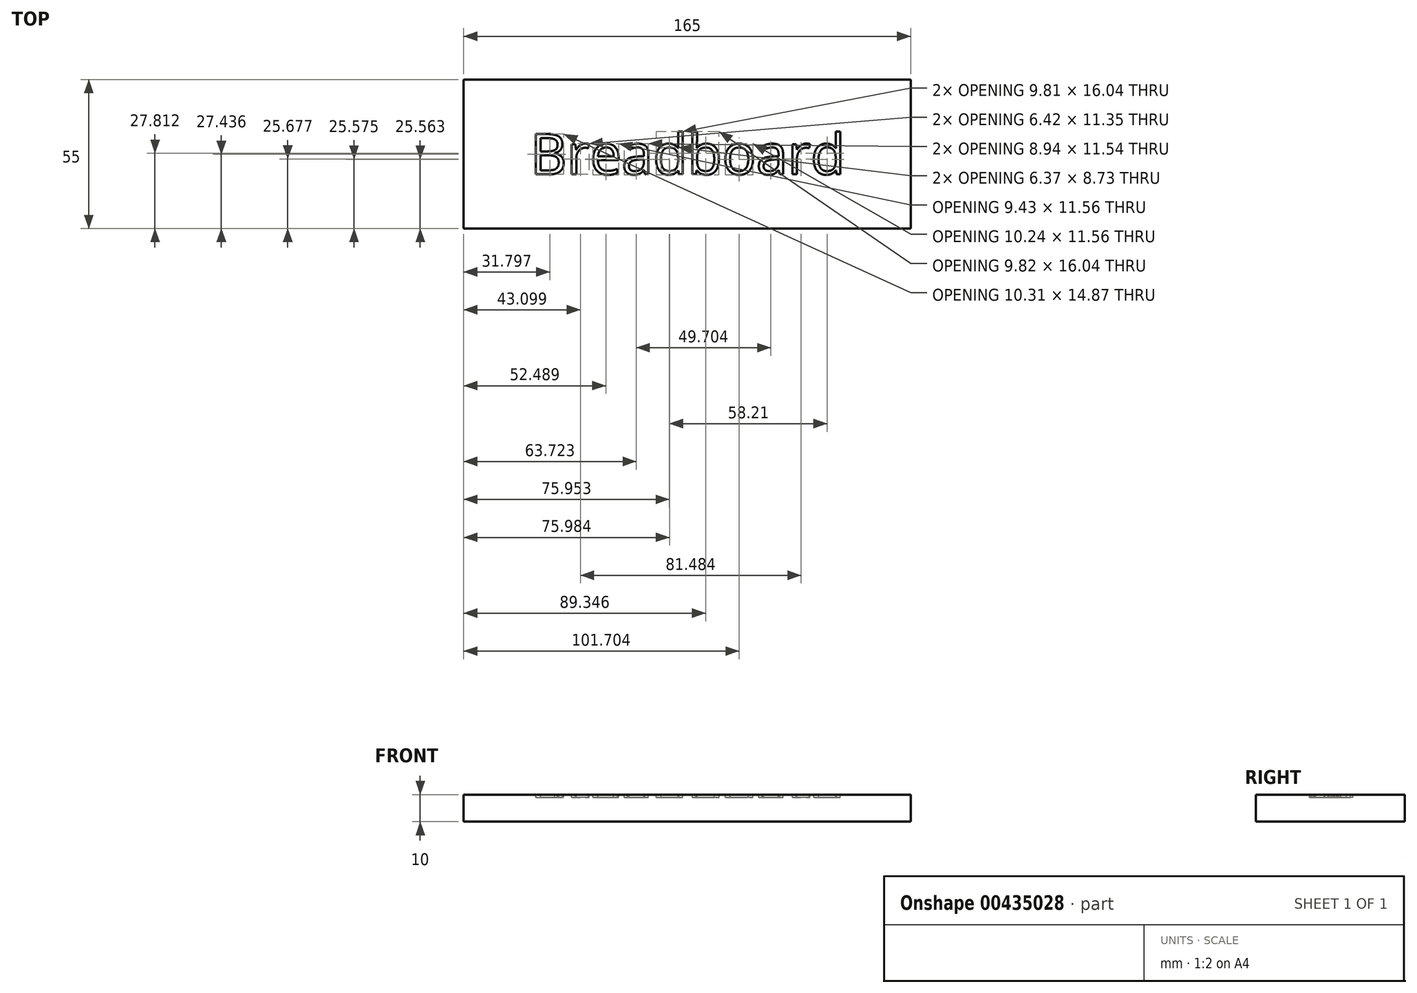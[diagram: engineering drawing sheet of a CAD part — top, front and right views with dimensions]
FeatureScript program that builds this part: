
annotation { "Feature Type Name" : "Feature", "Feature Type Description" : "" }
export const myFeature = defineFeature(function(context is Context, id is Id, definition is map)
    precondition{}
    {
        {
            var Q0;
            Q0=qCreatedBy(makeId("Top.planeOp"),FACE);
            var sketch = newSketch(context, id + "F0", { "sketchPlane" : qUnion([Q0])});
            skLineSegment(sketch, "E0.bottom", {"start": v(82.5, -27.5) * mm, "end": v(-82.5, -27.5) * mm});
            skLineSegment(sketch, "E0.top", {"start": v(82.5, 27.5) * mm, "end": v(-82.5, 27.5) * mm});
            skLineSegment(sketch, "E0.left", {"start": v(82.5, -27.5) * mm, "end": v(82.5, 27.5) * mm});
            skLineSegment(sketch, "E0.right", {"start": v(-82.5, -27.5) * mm, "end": v(-82.5, 27.5) * mm});
            skPoint(sketch, "E0.middle", {"position": v(0, 0) * mm});
            skSolve(sketch);
        }
        {
            var Q0;
            Q0=makeQuery(id+"F0.imprint","IMPRINT",FACE,{"disambiguationData":[TD([[makeQuery(id+"F0.imprint","IMPRINT",EDGE,{"derivedFrom":sQuery(id+"F0.wireOp",EDGE,"E0.bottom")}),-1.0]])]});
            extrude(context, id + "F1", {"entities" : qUnion([Q0]), "depth" : 10 * mm});
        }
        {
            var Q0;
            Q0=makeQuery(id+"F1.opExtrude","CAP_FACE",FACE,{"disambiguationData":[OSD([sQuery(id+"F0.wireOp",EDGE,"E0.bottom"),sQuery(id+"F0.wireOp",EDGE,"E0.top"),sQuery(id+"F0.wireOp",EDGE,"E0.left"),sQuery(id+"F0.wireOp",EDGE,"E0.right")])],"isStart":false});
            var sketch = newSketch(context, id + "F2", { "sketchPlane" : qUnion([Q0])});
            skText(sketch, "E1", { "text": "Breadboard", "fontName": "OpenSans-Regular.ttf"});
            const initialGuessF2  = {"E1": [-0.0579, -0.0075, 1, 0, 0.015]};
            skSetInitialGuess(sketch, initialGuessF2);
            skSolve(sketch);
        }
        {
            var Q0;
            Q0 = qSketchRegion(id + "F2", true);
            extrude(context, id + "F3", {"entities" : qUnion([Q0]), "operationType" : NewBodyOperationType.REMOVE, "oppositeDirection" : true, "depth" : 1 * mm});
        }
    });
